# Revit family: LRTH DFX
name_source: partatom
category: Lighting Fixtures
units: mm (PartAtom-declared; Revit-internal decimal feet)

## family parameters
Cut with Voids When Loaded = No
Host = Face
Light Source = Yes
Part Type = Normal
Room Calculation Point = No
Round Connector Dimension = Use Diameter
Shared = No

## types (10) — shared parameters
Assembly Code = D5020200
Color Filter = 16777215
Default Elevation = 4' - 0"
Description = LED Recessed with 365DisinFx UVA Technology
Dimming Lamp Color Temperature Shift = <None>
Emit Shape Visible in Rendering = No
Housing Finish = Metal - Viscor - White
Lamp = LED
Lens Finish = Acrylic - Viscor - Frosted Round
Manufacturer = VISIONEERING by VISCOR
Model = LRTH-DFX
Tilt Angle = -90.00°
URL = https://www.viscor.com
Voltage = 120 V

## per-type parameters (varying)
| type | Apparent Load | Cover Width | Emit from Rectangle Length | Emit from Rectangle Width | Lamp Wattage | Length | Photometric Web File | Width |
| LRTH-DFX2X2-LED840K032LUNV | 25 VA | 0' - 11 7/8" | 1' - 11 3/4" | 1' - 11 3/4" | 25 VA | 1' - 11 3/4" | LRTH-DFX2X2-LED840K032LUNV.ies | 1' - 11 3/4" |
| LRTH-DFX2X2-LED840K020LUNV | 16 VA | 0' - 11 7/8" | 1' - 11 3/4" | 1' - 11 3/4" | 16 VA | 1' - 11 3/4" | LRTH-DFX2X2-LED840K020LUNV.ies | 1' - 11 3/4" |
| LRTH-DFX2X4-LED840K032LUNV | 26 VA | 0' - 11 7/8" | 3' - 11 3/4" | 1' - 11 3/4" | 26 VA | 3' - 11 3/4" | LRTH-DFX2X4-LED840K032LUNV.ies | 1' - 11 3/4" |
| LRTH-DFX2X4-LED840K050LUNV | 44 VA | 0' - 11 7/8" | 3' - 11 3/4" | 1' - 11 3/4" | 44 VA | 3' - 11 3/4" | LRTH-DFX2X4-LED840K050LUNV.ies | 1' - 11 3/4" |
| LRTH-DFX2X4-LED840K060LUNV | 54 VA | 0' - 11 7/8" | 3' - 11 3/4" | 1' - 11 3/4" | 54 VA | 3' - 11 3/4" | LRTH-DFX2X4-LED840K060LUNV.ies | 1' - 11 3/4" |
| LRTH-DFX1X4-LED840K040LUNV | 33 VA | 0' - 5 7/8" | 3' - 11 3/4" | 0' - 11 3/4" | 33 VA | 3' - 11 3/4" | LRTH-DFX1X4-LED840K040LUNV.ies | 0' - 11 3/4" |
| LRTH-DFX1X4-LED840K032LUNV | 26 VA | 0' - 5 7/8" | 3' - 11 3/4" | 0' - 11 3/4" | 26 VA | 3' - 11 3/4" | LRTH-DFX1X4-LED840K032LUNV.ies | 0' - 11 3/4" |
| LRTH-DFX1X4-LED840K020LUNV | 16 VA | 0' - 5 7/8" | 3' - 11 3/4" | 0' - 11 3/4" | 16 VA | 3' - 11 3/4" | LRTH-DFX1X4-LED840K020LUNV.ies | 0' - 11 3/4" |
| LRTH-DFX2X4-LED840K040LUNV | 33 VA | 0' - 11 7/8" | 3' - 11 3/4" | 1' - 11 3/4" | 33 VA | 3' - 11 3/4" | LRTH-DFX2X4-LED840K040LUNV.ies | 1' - 11 3/4" |
| LRTH-DFX1X4-LED840K050LUNV | 44 VA | 0' - 5 7/8" | 3' - 11 3/4" | 0' - 11 3/4" | 44 VA | 3' - 11 3/4" | LRTH-DFX1X4-LED840K050LUNV.ies | 0' - 11 3/4" |

## geometry (parser evidence)
native form markers: Sweep x3
no freeform markers — native parametric forms only
